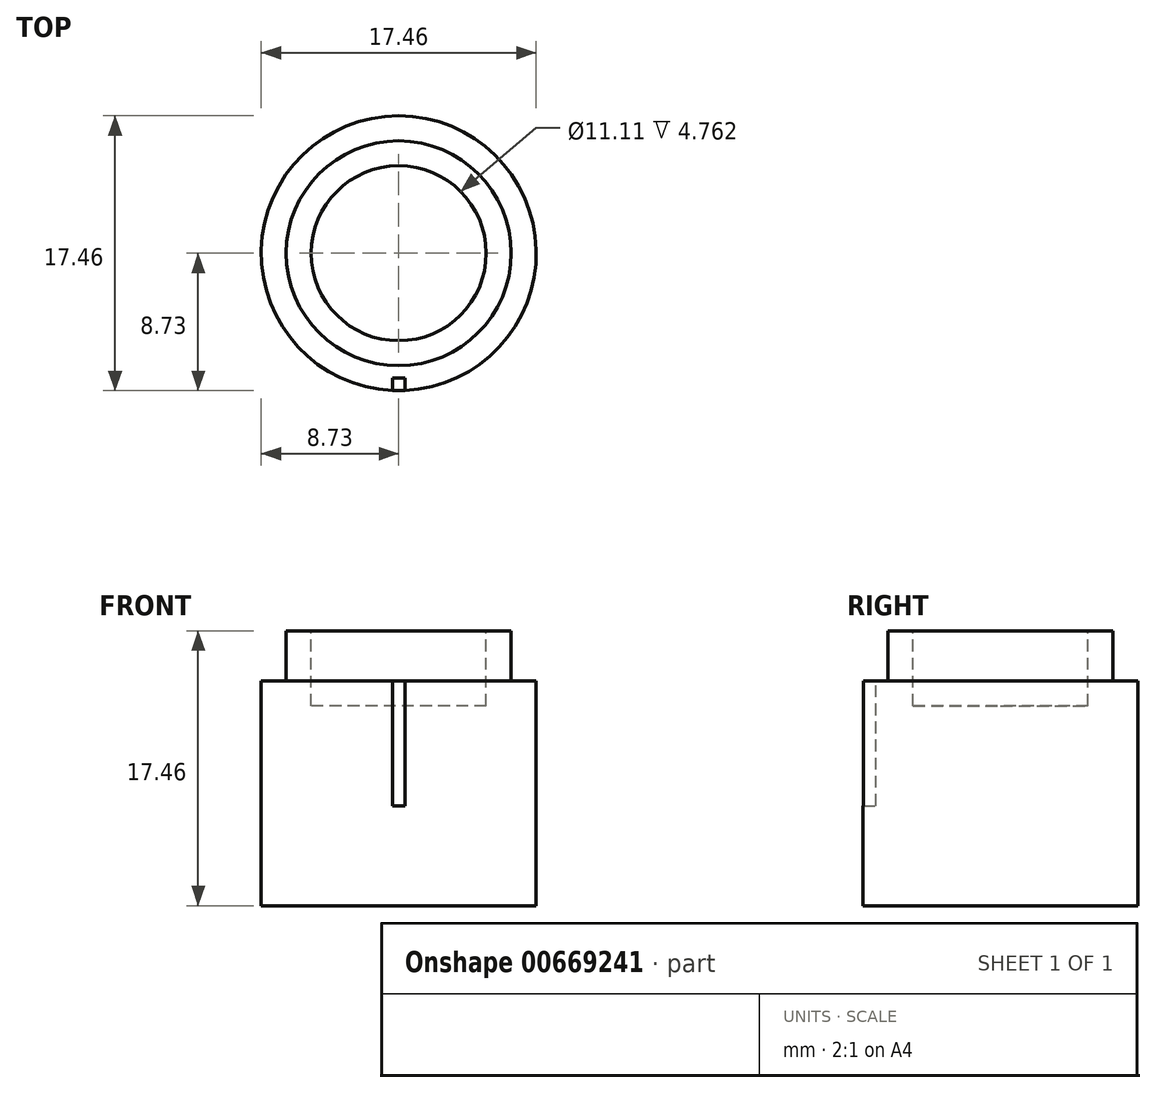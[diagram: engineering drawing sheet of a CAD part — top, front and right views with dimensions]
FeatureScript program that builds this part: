
annotation { "Feature Type Name" : "Feature", "Feature Type Description" : "" }
export const myFeature = defineFeature(function(context is Context, id is Id, definition is map)
    precondition{}
    {
        {
            var Q0;
            Q0=qCreatedBy(makeId("Top.planeOp"),FACE);
            var sketch = newSketch(context, id + "F0", { "sketchPlane" : qUnion([Q0])});
            skCircle(sketch, "E0", {"center": v(0, 0) * mm, "radius": 8.73 * mm});
            skSolve(sketch);
        }
        {
            var Q0;
            Q0 = qSketchRegion(id + "F0", true);
            extrude(context, id + "F1", {"entities" : qUnion([Q0]), "depth" : 17.46 * mm, "offsetDistance" : 25.4 * mm});
        }
        {
            var Q0;
            Q0=makeQuery(id+"F1.opExtrude","CAP_FACE",FACE,{"disambiguationData":[OSD([sQuery(id+"F0.wireOp",EDGE,"E0")])],"isStart":false});
            var sketch = newSketch(context, id + "F2", { "sketchPlane" : qUnion([Q0])});
            skCircle(sketch, "E1", {"center": v(0, 0) * mm, "radius": 5.56 * mm});
            skSolve(sketch);
        }
        {
            var Q0;
            Q0 = qSketchRegion(id + "F2", true);
            extrude(context, id + "F3", {"entities" : qUnion([Q0]), "operationType" : NewBodyOperationType.REMOVE, "oppositeDirection" : true, "depth" : 4.76 * mm, "offsetDistance" : 25.4 * mm});
        }
        {
            var Q0;
            Q0=makeQuery(id+"F1.opExtrude","CAP_FACE",FACE,{"disambiguationData":[OSD([sQuery(id+"F0.wireOp",EDGE,"E0")])],"isStart":false});
            var sketch = newSketch(context, id + "F4", { "sketchPlane" : qUnion([Q0])});
            skCircle(sketch, "E2", {"center": v(0, 0) * mm, "radius": 7.14 * mm});
            skCircle(sketch, "E3", {"center": v(0, 0) * mm, "radius": 8.73 * mm});
            skPoint(sketch, "E3.first.point", {"position": v(-8.73, 0) * mm});
            skPoint(sketch, "E3.second.point", {"position": v(8.73, 0) * mm});
            skPoint(sketch, "E3.third.point", {"position": v(0, 8.73) * mm});
            skSolve(sketch);
        }
        {
            var Q0;
            Q0 = qSketchRegion(id + "F4", true);
            extrude(context, id + "F5", {"entities" : qUnion([Q0]), "operationType" : NewBodyOperationType.REMOVE, "oppositeDirection" : true, "depth" : 3.17 * mm, "offsetDistance" : 25.4 * mm});
        }
        {
            var Q0;
            Q0=makeQuery(id+"F5.boolean.opBoolean","COPY",FACE,{"derivedFrom":makeQuery(id+"F5.opExtrude","CAP_FACE",FACE,{"disambiguationData":[OSD([sQuery(id+"F4.wireOp",EDGE,"E2"),sQuery(id+"F4.wireOp",EDGE,"E3")])],"isStart":false})});
            var sketch = newSketch(context, id + "F6", { "sketchPlane" : qUnion([Q0])});
            skLineSegment(sketch, "E4.left", {"start": v(-0.4, -8.72) * mm, "end": v(-0.4, -7.93) * mm});
            skLineSegment(sketch, "E4.right", {"start": v(0.4, -8.72) * mm, "end": v(0.4, -7.92) * mm});
            skPoint(sketch, "E5", {"position": v(0, -8.73) * mm});
            skArc(sketch, "E6", {"start": v(-0.4, -8.72) * mm, "mid": v(0, -8.73) * mm, "end": v(0.4, -8.72) * mm});
            skArc(sketch, "E7", {"start": v(-0.4, -7.93) * mm, "mid": v(0, -7.93) * mm, "end": v(0.4, -7.92) * mm});
            skSolve(sketch);
        }
        {
            var Q0;
            Q0 = qSketchRegion(id + "F6", true);
            extrude(context, id + "F7", {"entities" : qUnion([Q0]), "operationType" : NewBodyOperationType.REMOVE, "oppositeDirection" : true, "depth" : 7.94 * mm, "offsetDistance" : 25.4 * mm});
        }
    });
